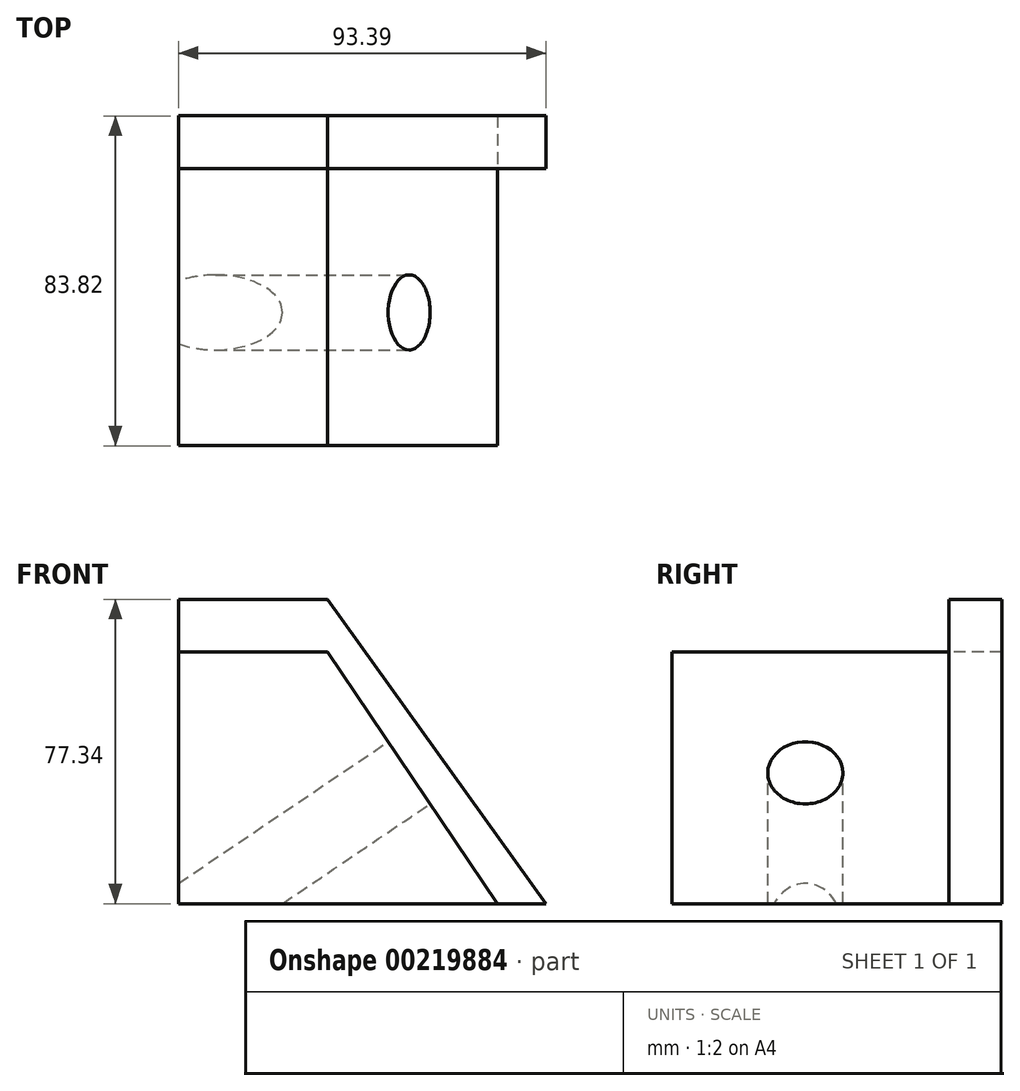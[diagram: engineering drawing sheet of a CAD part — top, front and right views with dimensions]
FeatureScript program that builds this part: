
annotation { "Feature Type Name" : "Feature", "Feature Type Description" : "" }
export const myFeature = defineFeature(function(context is Context, id is Id, definition is map)
    precondition{}
    {
        {
            var Q0;
            Q0=qCreatedBy(makeId("Front.planeOp"),FACE);
            var sketch = newSketch(context, id + "F0", { "sketchPlane" : qUnion([Q0])});
            skLineSegment(sketch, "E0", {"start": v(-34.4, -23.9) * mm, "end": v(46.64, -23.9) * mm});
            skLineSegment(sketch, "E1", {"start": v(46.64, -23.9) * mm, "end": v(3.46, 40.06) * mm});
            skLineSegment(sketch, "E2", {"start": v(3.46, 40.06) * mm, "end": v(-34.4, 40.06) * mm});
            skLineSegment(sketch, "E3", {"start": v(-34.4, 40.06) * mm, "end": v(-34.4, -23.9) * mm});
            skSolve(sketch);
        }
        {
            var Q0;
            Q0 = qSketchRegion(id + "F0", true);
            extrude(context, id + "F1", {"entities" : qUnion([Q0]), "depth" : 70.36 * mm});
        }
        {
            var Q0;
            Q0=makeQuery(id+"F1.opExtrude","SWEPT_FACE",FACE,{"disambiguationData":[OSD([sQuery(id+"F0.wireOp",EDGE,"E1")])]});
            var sketch = newSketch(context, id + "F2", { "sketchPlane" : qUnion([Q0])});
            skCircle(sketch, "E4", {"center": v(-36.48, -5.81) * mm, "radius": 10.8 * mm});
            skSolve(sketch);
        }
        {
            var Q0;
            Q0=sQuery(id+"F2.wireOp",VERTEX,"E4.center");
            var Q1;
            Q1=makeQuery(id+"F1.opExtrude","SWEPT_BODY",BODY,{"disambiguationData":[OSD([sQuery(id+"F0.wireOp",EDGE,"E0"),sQuery(id+"F0.wireOp",EDGE,"E1"),sQuery(id+"F0.wireOp",EDGE,"E2"),sQuery(id+"F0.wireOp",EDGE,"E3")])]});
            hole(context, id + "F3", {"style" : HoleStyle.SIMPLE, "endStyle" : HoleEndStyle.THROUGH, "holeDiameter" : 19.05 * mm, "locations" : qUnion([Q0]), "scope" : qUnion([Q1]), "isTappedThrough" : true});
        }
        {
            var Q0;
            Q0=makeQuery(id+"F1.opExtrude","CAP_FACE",FACE,{"disambiguationData":[OSD([sQuery(id+"F0.wireOp",EDGE,"E0"),sQuery(id+"F0.wireOp",EDGE,"E1"),sQuery(id+"F0.wireOp",EDGE,"E2"),sQuery(id+"F0.wireOp",EDGE,"E3")])],"isStart":true});
            var sketch = newSketch(context, id + "F4", { "sketchPlane" : qUnion([Q0])});
            skLineSegment(sketch, "E5", {"start": v(34.4, 40.06) * mm, "end": v(34.4, 53.44) * mm});
            skLineSegment(sketch, "E6", {"start": v(34.4, 53.44) * mm, "end": v(-3.46, 53.44) * mm});
            skLineSegment(sketch, "E7", {"start": v(-3.46, 53.44) * mm, "end": v(-58.98, -23.9) * mm});
            skLineSegment(sketch, "E8", {"start": v(-58.98, -23.9) * mm, "end": v(-46.64, -23.9) * mm});
            skSolve(sketch);
        }
        {
            var Q0;
            Q0=makeQuery(id+"F4.imprint","IMPRINT",FACE,{"disambiguationData":[TD([[makeQuery(id+"F4.imprint","IMPRINT",EDGE,{"derivedFrom":sQuery(id+"F4.wireOp",EDGE,"E5")}),1.0]])]});
            extrude(context, id + "F5", {"entities" : qUnion([Q0]), "depth" : 13.46 * mm});
        }
    });
